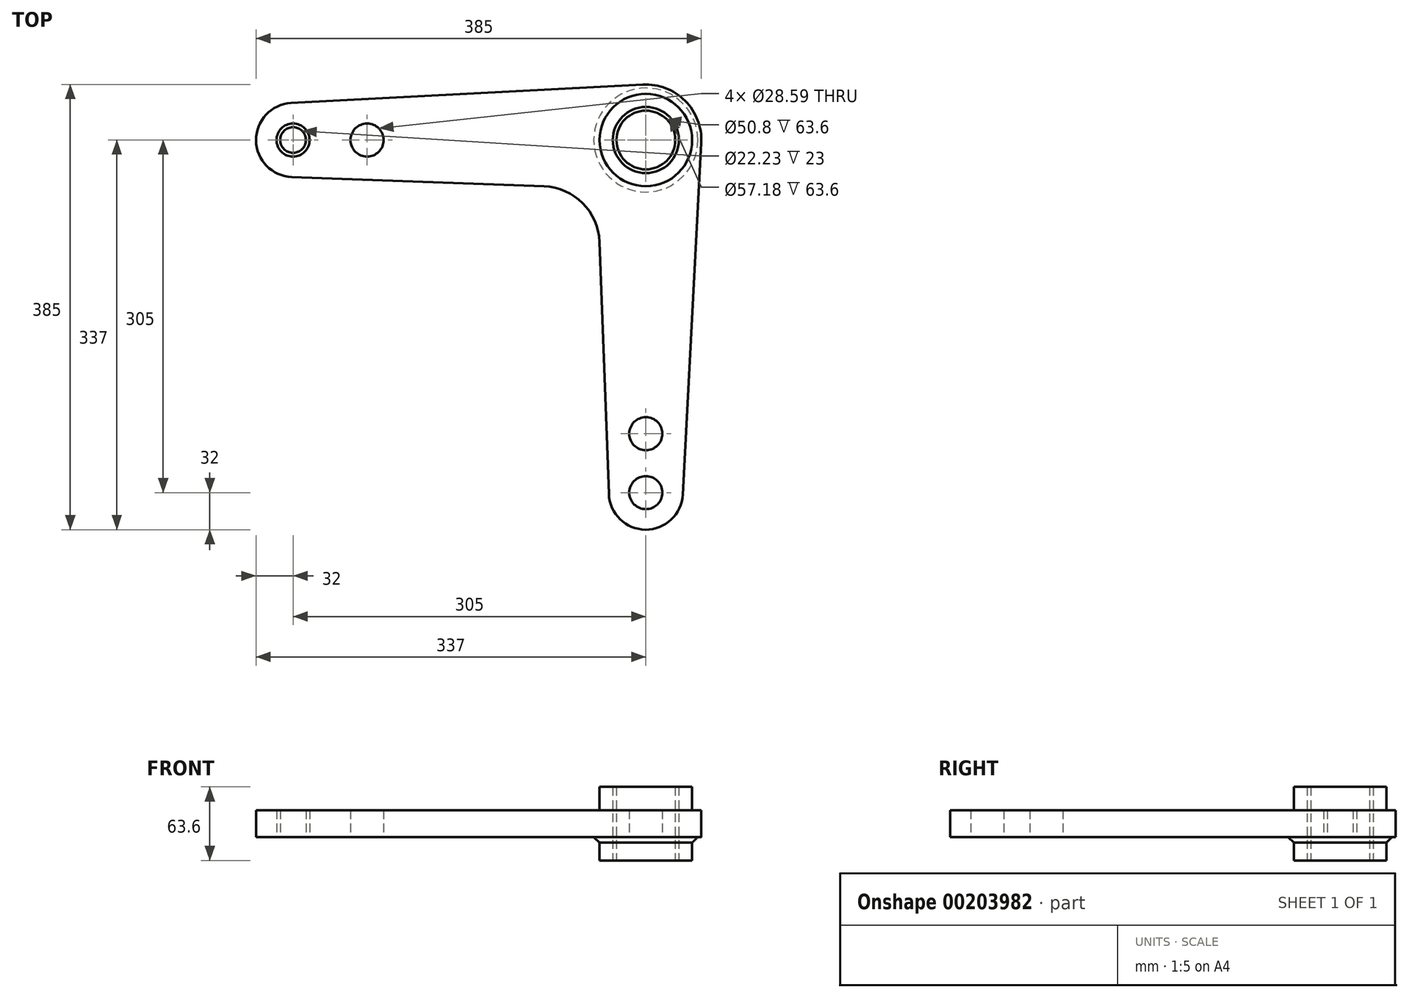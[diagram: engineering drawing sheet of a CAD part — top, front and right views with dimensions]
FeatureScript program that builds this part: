
annotation { "Feature Type Name" : "Feature", "Feature Type Description" : "" }
export const myFeature = defineFeature(function(context is Context, id is Id, definition is map)
    precondition{}
    {
        {
            var Q0;
            Q0=qCreatedBy(makeId("Top.planeOp"),FACE);
            var sketch = newSketch(context, id + "F0", { "sketchPlane" : qUnion([Q0])});
            skLineSegment(sketch, "E0", {"start": v(0, 0) * mm, "end": v(-305, 0) * mm, "construction": true});
            skLineSegment(sketch, "E1", {"start": v(0, -305) * mm, "end": v(0, 0) * mm, "construction": true});
            skPoint(sketch, "E2", {"position": v(-241, 0) * mm});
            skPoint(sketch, "E3", {"position": v(0, -254) * mm});
            skArc(sketch, "E4", {"start": v(-31.98, -306.18) * mm, "mid": v(-0.25, -337) * mm, "end": v(31.96, -306.68) * mm});
            skArc(sketch, "E5", {"start": v(-306.68, 31.96) * mm, "mid": v(-337, -0.25) * mm, "end": v(-306.18, -31.98) * mm});
            skPoint(sketch, "E6", {"position": v(-90, -90) * mm});
            skArc(sketch, "E7", {"start": v(-2.52, 47.93) * mm, "mid": v(33.94, 33.94) * mm, "end": v(47.93, -2.52) * mm});
            skLineSegment(sketch, "E8", {"start": v(31.96, -306.68) * mm, "end": v(47.93, -2.52) * mm});
            skPoint(sketch, "E9.orphan", {"position": v(-40, -90) * mm});
            skPoint(sketch, "E10.start.orphan", {"position": v(-90, -40) * mm});
            skArc(sketch, "E11", {"start": v(-40, -90) * mm, "mid": v(-54.64, -54.64) * mm, "end": v(-90, -40) * mm});
            skLineSegment(sketch, "E12", {"start": v(-40.03, -88.15) * mm, "end": v(-31.98, -306.18) * mm});
            skLineSegment(sketch, "E13", {"start": v(-306.68, 31.96) * mm, "end": v(-2.52, 47.93) * mm});
            skLineSegment(sketch, "E14", {"start": v(-88.15, -40.03) * mm, "end": v(-306.18, -31.98) * mm});
            skCircle(sketch, "E15", {"center": v(0, -305) * mm, "radius": 14.3 * mm});
            skCircle(sketch, "E16", {"center": v(0, -254) * mm, "radius": 14.3 * mm});
            skCircle(sketch, "E17", {"center": v(-305, 0) * mm, "radius": 14.3 * mm});
            skCircle(sketch, "E18", {"center": v(-241, 0) * mm, "radius": 14.3 * mm});
            skCircle(sketch, "E19", {"center": v(0, 0) * mm, "radius": 28.6 * mm});
            skCircle(sketch, "E20", {"center": v(0, 0) * mm, "radius": 40 * mm});
            skCircle(sketch, "E21", {"center": v(-305, 0) * mm, "radius": 11.11 * mm});
            skCircle(sketch, "E22", {"center": v(0, 0) * mm, "radius": 25.4 * mm});
            skSolve(sketch);
        }
        {
            var Q0;
            Q0=makeQuery(id+"F0.imprint","IMPRINT",FACE,{"disambiguationData":[TD([[makeQuery(id+"F0.imprint","IMPRINT",EDGE,{"derivedFrom":sQuery(id+"F0.wireOp",EDGE,"E4")}),1.0]])]});
            extrude(context, id + "F1", {"entities" : qUnion([Q0]), "endBound" : BoundingType.SYMMETRIC, "depth" : 23 * mm});
        }
        {
            var Q0;
            Q0=makeQuery(id+"F0.imprint","IMPRINT",FACE,{"disambiguationData":[TD([[makeQuery(id+"F0.imprint","IMPRINT",EDGE,{"derivedFrom":sQuery(id+"F0.wireOp",EDGE,"E19")}),-1.0]])]});
            extrude(context, id + "F2", {"entities" : qUnion([Q0]), "operationType" : NewBodyOperationType.ADD, "endBound" : BoundingType.SYMMETRIC, "depth" : 63.6 * mm});
        }
        {
            var Q0;
            Q0=makeQuery(id+"F1.opExtrude","CAP_EDGE",EDGE,{"disambiguationData":[OSD([sQuery(id+"F0.wireOp",EDGE,"E20")])],"isStart":true});
            var Q1;
            Q1=makeQuery(id+"F1.opExtrude","CAP_EDGE",EDGE,{"disambiguationData":[OSD([sQuery(id+"F0.wireOp",EDGE,"E20")])],"isStart":false});
            chamfer(context, id + "F3", {"entities" : qUnion([Q0, Q1]), "width" : 5 * mm, "tangentPropagation" : true});
        }
        {
            var Q0;
            Q0=makeQuery(id+"F0.imprint","IMPRINT",FACE,{"disambiguationData":[TD([[makeQuery(id+"F0.imprint","IMPRINT",EDGE,{"derivedFrom":sQuery(id+"F0.wireOp",EDGE,"E17")}),1.0]])]});
            extrude(context, id + "F4", {"entities" : qUnion([Q0]), "endBound" : BoundingType.SYMMETRIC, "depth" : 23 * mm});
        }
        {
            var Q0;
            Q0=makeQuery(id+"F0.imprint","IMPRINT",FACE,{"disambiguationData":[TD([[makeQuery(id+"F0.imprint","IMPRINT",EDGE,{"derivedFrom":sQuery(id+"F0.wireOp",EDGE,"E19")}),1.0]])]});
            extrude(context, id + "F5", {"entities" : qUnion([Q0]), "endBound" : BoundingType.SYMMETRIC, "depth" : 63.6 * mm});
        }
    });
